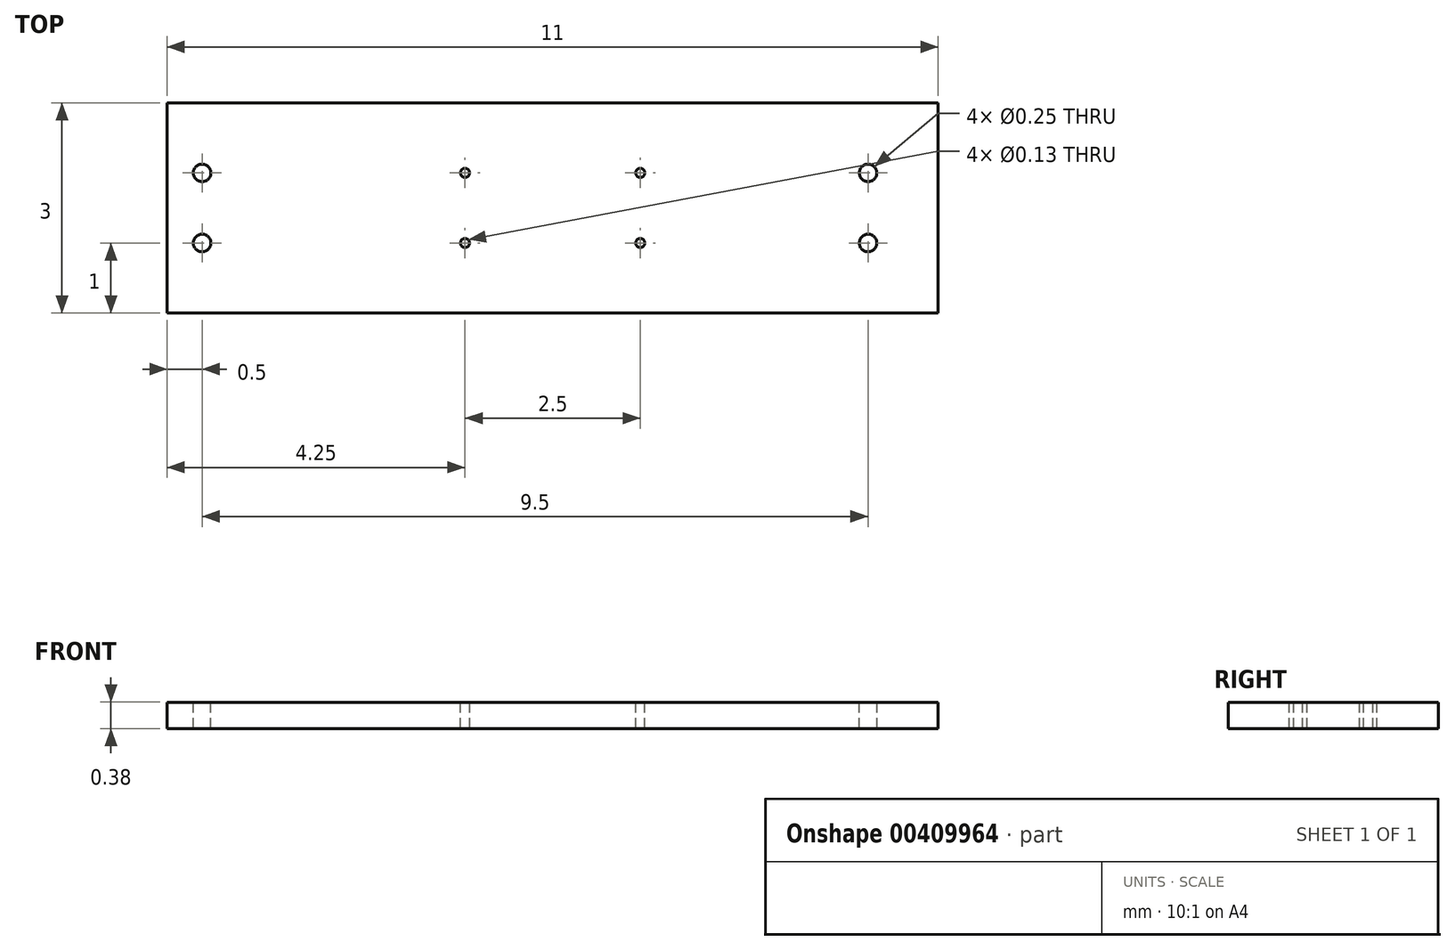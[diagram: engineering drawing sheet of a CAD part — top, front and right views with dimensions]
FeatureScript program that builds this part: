
annotation { "Feature Type Name" : "Feature", "Feature Type Description" : "" }
export const myFeature = defineFeature(function(context is Context, id is Id, definition is map)
    precondition{}
    {
        {
            var Q0;
            Q0=qCreatedBy(makeId("Top.planeOp"),FACE);
            var sketch = newSketch(context, id + "F0", { "sketchPlane" : qUnion([Q0])});
            skLineSegment(sketch, "E0.bottom", {"start": v(-6, 1.5) * mm, "end": v(5, 1.5) * mm});
            skLineSegment(sketch, "E0.top", {"start": v(-6, -1.5) * mm, "end": v(5, -1.5) * mm});
            skLineSegment(sketch, "E0.left", {"start": v(-6, 1.5) * mm, "end": v(-6, -1.5) * mm});
            skLineSegment(sketch, "E0.right", {"start": v(5, 1.5) * mm, "end": v(5, -1.5) * mm});
            skSolve(sketch);
        }
        {
            var Q0;
            Q0 = qSketchRegion(id + "F0", true);
            extrude(context, id + "F1", {"entities" : qUnion([Q0]), "depth" : 0.38 * mm});
        }
        {
            var Q0;
            Q0=makeQuery(id+"F1.opExtrude","CAP_FACE",FACE,{"disambiguationData":[OSD([sQuery(id+"F0.wireOp",EDGE,"E0.bottom"),sQuery(id+"F0.wireOp",EDGE,"E0.top"),sQuery(id+"F0.wireOp",EDGE,"E0.left"),sQuery(id+"F0.wireOp",EDGE,"E0.right")])],"isStart":false});
            var sketch = newSketch(context, id + "F2", { "sketchPlane" : qUnion([Q0])});
            skLineSegment(sketch, "E1", {"start": v(-3.95, 0.5) * mm, "end": v(4.56, 0.5) * mm, "construction": true});
            skLineSegment(sketch, "E2", {"start": v(-3.99, -0.5) * mm, "end": v(4.18, -0.5) * mm, "construction": true});
            skCircle(sketch, "E3", {"center": v(-5.5, 0.5) * mm, "radius": 0.12 * mm});
            skCircle(sketch, "E4", {"center": v(-5.5, -0.5) * mm, "radius": 0.12 * mm});
            skCircle(sketch, "E5", {"center": v(-1.75, 0.5) * mm, "radius": 0.07 * mm});
            skCircle(sketch, "E6", {"center": v(-1.75, -0.5) * mm, "radius": 0.07 * mm});
            skCircle(sketch, "E7", {"center": v(0.75, 0.5) * mm, "radius": 0.07 * mm});
            skCircle(sketch, "E8", {"center": v(0.75, -0.5) * mm, "radius": 0.07 * mm});
            skCircle(sketch, "E9", {"center": v(4, 0.5) * mm, "radius": 0.12 * mm});
            skCircle(sketch, "E10", {"center": v(4, -0.5) * mm, "radius": 0.12 * mm});
            skSolve(sketch);
        }
        {
            var Q0;
            Q0 = qSketchRegion(id + "F2", true);
            extrude(context, id + "F3", {"entities" : qUnion([Q0]), "operationType" : NewBodyOperationType.REMOVE, "oppositeDirection" : true, "depth" : 2 * mm});
        }
    });
